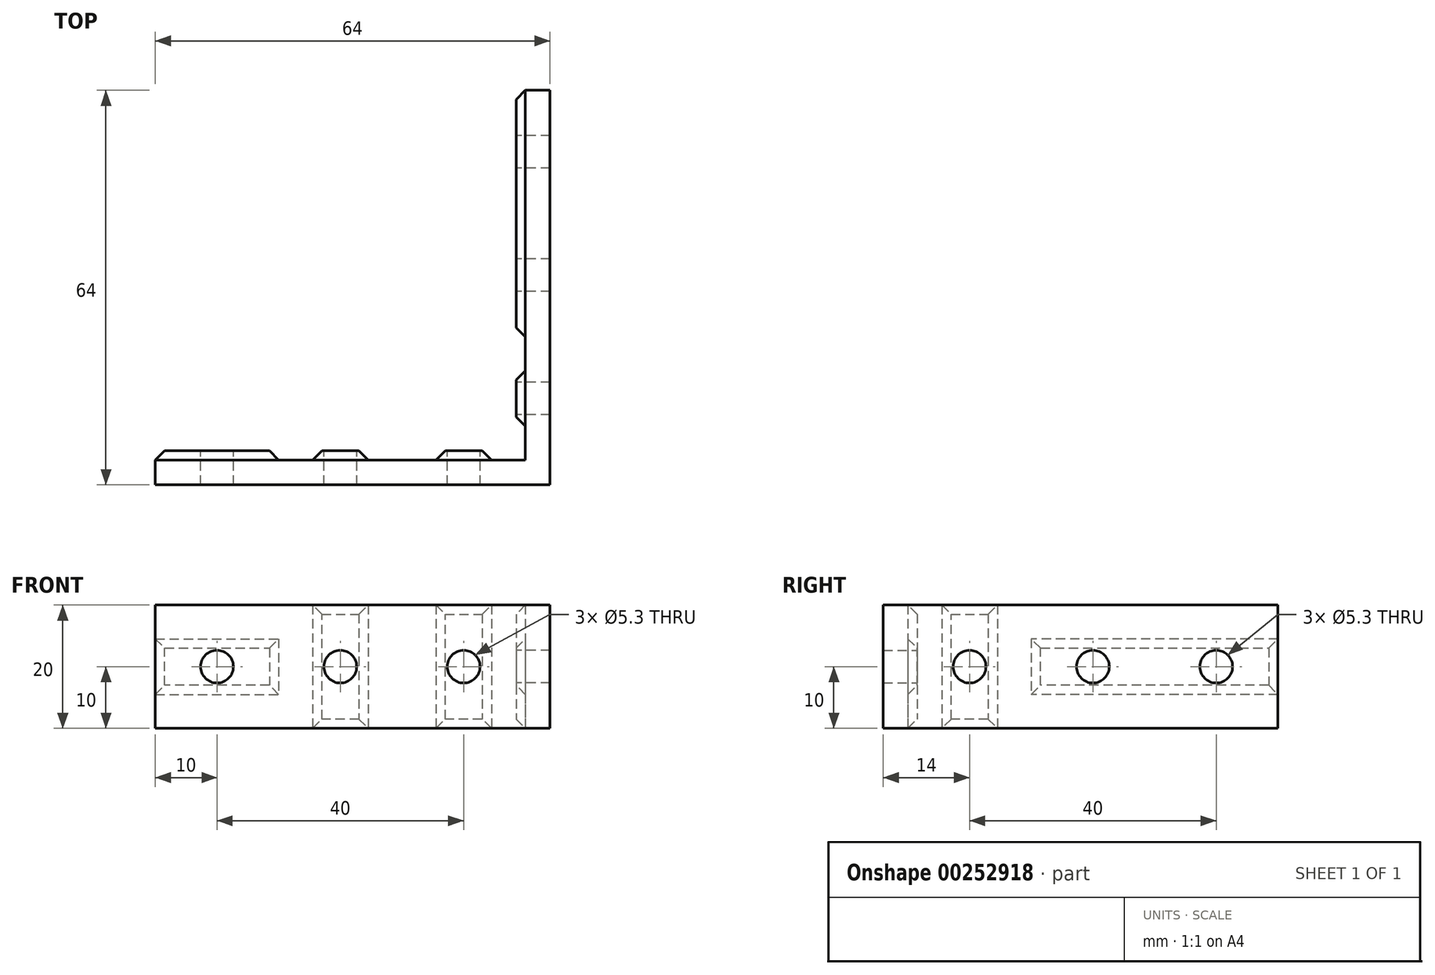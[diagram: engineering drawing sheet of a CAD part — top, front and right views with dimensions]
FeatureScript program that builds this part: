
annotation { "Feature Type Name" : "Feature", "Feature Type Description" : "" }
export const myFeature = defineFeature(function(context is Context, id is Id, definition is map)
    precondition{}
    {
        {
            var Q0;
            Q0=qCreatedBy(makeId("Top.planeOp"),FACE);
            var sketch = newSketch(context, id + "F0", { "sketchPlane" : qUnion([Q0])});
            skLineSegment(sketch, "E0", {"start": v(0, 0) * mm, "end": v(0, 64) * mm});
            skLineSegment(sketch, "E1", {"start": v(0, 64) * mm, "end": v(-4, 64) * mm});
            skLineSegment(sketch, "E2", {"start": v(-4, 64) * mm, "end": v(-4, 4) * mm});
            skLineSegment(sketch, "E3", {"start": v(-4, 4) * mm, "end": v(-64, 4) * mm});
            skLineSegment(sketch, "E4", {"start": v(-64, 4) * mm, "end": v(-64, 0) * mm});
            skLineSegment(sketch, "E5", {"start": v(-64, 0) * mm, "end": v(0, 0) * mm});
            skSolve(sketch);
        }
        {
            var Q0;
            Q0 = qSketchRegion(id + "F0", true);
            extrude(context, id + "F1", {"entities" : qUnion([Q0]), "depth" : 20 * mm});
        }
        {
            var Q0;
            Q0=makeQuery(id+"F1.opExtrude","SWEPT_FACE",FACE,{"disambiguationData":[OSD([sQuery(id+"F0.wireOp",EDGE,"E3")])]});
            var sketch = newSketch(context, id + "F2", { "sketchPlane" : qUnion([Q0])});
            skLineSegment(sketch, "E6.bottom", {"start": v(9.5, 20) * mm, "end": v(18.5, 20) * mm});
            skLineSegment(sketch, "E6.top", {"start": v(9.5, 0) * mm, "end": v(18.5, 0) * mm});
            skLineSegment(sketch, "E6.left", {"start": v(9.5, 20) * mm, "end": v(9.5, 0) * mm});
            skLineSegment(sketch, "E6.right", {"start": v(18.5, 20) * mm, "end": v(18.5, 0) * mm});
            skLineSegment(sketch, "E7.bottom", {"start": v(29.5, 20) * mm, "end": v(38.5, 20) * mm});
            skLineSegment(sketch, "E7.top", {"start": v(29.5, 0) * mm, "end": v(38.5, 0) * mm});
            skLineSegment(sketch, "E7.left", {"start": v(29.5, 20) * mm, "end": v(29.5, 0) * mm});
            skLineSegment(sketch, "E7.right", {"start": v(38.5, 20) * mm, "end": v(38.5, 0) * mm});
            skLineSegment(sketch, "E8.bottom", {"start": v(64, 14.5) * mm, "end": v(44, 14.5) * mm});
            skLineSegment(sketch, "E8.top", {"start": v(64, 5.5) * mm, "end": v(44, 5.5) * mm});
            skLineSegment(sketch, "E8.left", {"start": v(64, 14.5) * mm, "end": v(64, 5.5) * mm});
            skLineSegment(sketch, "E8.right", {"start": v(44, 14.5) * mm, "end": v(44, 5.5) * mm});
            skSolve(sketch);
        }
        {
            var Q0;
            Q0 = qSketchRegion(id + "F2", true);
            extrude(context, id + "F3", {"entities" : qUnion([Q0]), "operationType" : NewBodyOperationType.ADD, "depth" : 1.5 * mm});
        }
        {
            var Q0;
            Q0=makeQuery(id+"F1.opExtrude","SWEPT_FACE",FACE,{"disambiguationData":[OSD([sQuery(id+"F0.wireOp",EDGE,"E2")])]});
            var sketch = newSketch(context, id + "F4", { "sketchPlane" : qUnion([Q0])});
            skLineSegment(sketch, "E9.bottom", {"start": v(-64, 14.5) * mm, "end": v(-24, 14.5) * mm});
            skLineSegment(sketch, "E9.top", {"start": v(-64, 5.5) * mm, "end": v(-24, 5.5) * mm});
            skLineSegment(sketch, "E9.left", {"start": v(-64, 14.5) * mm, "end": v(-64, 5.5) * mm});
            skLineSegment(sketch, "E9.right", {"start": v(-24, 14.5) * mm, "end": v(-24, 5.5) * mm});
            skLineSegment(sketch, "E10.bottom", {"start": v(-9.5, 20) * mm, "end": v(-18.5, 20) * mm});
            skLineSegment(sketch, "E10.top", {"start": v(-9.5, 0) * mm, "end": v(-18.5, 0) * mm});
            skLineSegment(sketch, "E10.left", {"start": v(-9.5, 20) * mm, "end": v(-9.5, 0) * mm});
            skLineSegment(sketch, "E10.right", {"start": v(-18.5, 20) * mm, "end": v(-18.5, 0) * mm});
            skSolve(sketch);
        }
        {
            var Q0;
            Q0 = qSketchRegion(id + "F4", true);
            extrude(context, id + "F5", {"entities" : qUnion([Q0]), "operationType" : NewBodyOperationType.ADD, "depth" : 1.5 * mm});
        }
        {
            var Q0;
            Q0=makeQuery(id+"F5.opExtrude","CAP_EDGE",EDGE,{"disambiguationData":[OSD([sQuery(id+"F4.wireOp",EDGE,"E9.left")])],"isStart":false});
            var Q1;
            Q1=makeQuery(id+"F5.opExtrude","CAP_EDGE",EDGE,{"disambiguationData":[OSD([sQuery(id+"F4.wireOp",EDGE,"E9.bottom")])],"isStart":false});
            var Q2;
            Q2=makeQuery(id+"F5.opExtrude","CAP_EDGE",EDGE,{"disambiguationData":[OSD([sQuery(id+"F4.wireOp",EDGE,"E9.top")])],"isStart":false});
            var Q3;
            Q3=makeQuery(id+"F5.opExtrude","CAP_EDGE",EDGE,{"disambiguationData":[OSD([sQuery(id+"F4.wireOp",EDGE,"E9.right")])],"isStart":false});
            var Q4;
            Q4=makeQuery(id+"F3.opExtrude","CAP_EDGE",EDGE,{"disambiguationData":[OSD([sQuery(id+"F2.wireOp",EDGE,"E8.bottom")])],"isStart":false});
            var Q5;
            Q5=makeQuery(id+"F3.opExtrude","CAP_EDGE",EDGE,{"disambiguationData":[OSD([sQuery(id+"F2.wireOp",EDGE,"E8.top")])],"isStart":false});
            var Q6;
            Q6=makeQuery(id+"F3.opExtrude","CAP_EDGE",EDGE,{"disambiguationData":[OSD([sQuery(id+"F2.wireOp",EDGE,"E8.right")])],"isStart":false});
            var Q7;
            Q7=makeQuery(id+"F3.opExtrude","CAP_EDGE",EDGE,{"disambiguationData":[OSD([sQuery(id+"F2.wireOp",EDGE,"E8.left")])],"isStart":false});
            var Q8;
            Q8=makeQuery(id+"F3.opExtrude","CAP_FACE",FACE,{"disambiguationData":[OSD([sQuery(id+"F2.wireOp",EDGE,"E7.bottom"),sQuery(id+"F2.wireOp",EDGE,"E7.top"),sQuery(id+"F2.wireOp",EDGE,"E7.left"),sQuery(id+"F2.wireOp",EDGE,"E7.right")])],"isStart":false});
            var Q9;
            Q9=makeQuery(id+"F3.opExtrude","CAP_FACE",FACE,{"disambiguationData":[OSD([sQuery(id+"F2.wireOp",EDGE,"E6.bottom"),sQuery(id+"F2.wireOp",EDGE,"E6.top"),sQuery(id+"F2.wireOp",EDGE,"E6.left"),sQuery(id+"F2.wireOp",EDGE,"E6.right")])],"isStart":false});
            var Q10;
            Q10=makeQuery(id+"F5.opExtrude","CAP_FACE",FACE,{"disambiguationData":[OSD([sQuery(id+"F4.wireOp",EDGE,"E10.bottom"),sQuery(id+"F4.wireOp",EDGE,"E10.top"),sQuery(id+"F4.wireOp",EDGE,"E10.left"),sQuery(id+"F4.wireOp",EDGE,"E10.right")])],"isStart":false});
            chamfer(context, id + "F6", {"entities" : qUnion([Q0, Q1, Q2, Q3, Q4, Q5, Q6, Q7, Q8, Q9, Q10]), "width" : 1.5 * mm, "tangentPropagation" : true});
        }
        {
            var Q0;
            Q0=makeQuery(id+"F3.opExtrude","CAP_FACE",FACE,{"disambiguationData":[OSD([sQuery(id+"F2.wireOp",EDGE,"E6.bottom"),sQuery(id+"F2.wireOp",EDGE,"E6.top"),sQuery(id+"F2.wireOp",EDGE,"E6.left"),sQuery(id+"F2.wireOp",EDGE,"E6.right")])],"isStart":false});
            var sketch = newSketch(context, id + "F7", { "sketchPlane" : qUnion([Q0])});
            skCircle(sketch, "E11", {"center": v(14, 10) * mm, "radius": 2.65 * mm});
            skPoint(sketch, "E11.centerSnap0", {"position": v(17, 10) * mm});
            skPoint(sketch, "E11.centerSnap1", {"position": v(14, 18.5) * mm});
            skLineSegment(sketch, "E12.0.0", {"start": v(31, 18.5) * mm, "end": v(31, 1.5) * mm, "construction": true});
            skLineSegment(sketch, "E12.0.1", {"start": v(31, 1.5) * mm, "end": v(37, 1.5) * mm, "construction": true});
            skLineSegment(sketch, "E12.0.2", {"start": v(37, 1.5) * mm, "end": v(37, 18.5) * mm, "construction": true});
            skLineSegment(sketch, "E12.0.3", {"start": v(37, 18.5) * mm, "end": v(31, 18.5) * mm, "construction": true});
            skLineSegment(sketch, "E13.0.0", {"start": v(45.5, 13) * mm, "end": v(45.5, 7) * mm, "construction": true});
            skLineSegment(sketch, "E13.0.1", {"start": v(45.5, 7) * mm, "end": v(62.5, 7) * mm, "construction": true});
            skLineSegment(sketch, "E13.0.2", {"start": v(62.5, 7) * mm, "end": v(62.5, 13) * mm, "construction": true});
            skLineSegment(sketch, "E13.0.3", {"start": v(62.5, 13) * mm, "end": v(45.5, 13) * mm, "construction": true});
            skPoint(sketch, "E14.centerSnap0", {"position": v(37, 10) * mm});
            skPoint(sketch, "E14.centerSnap1", {"position": v(34, 18.5) * mm});
            skCircle(sketch, "E15", {"center": v(34, 10) * mm, "radius": 2.65 * mm});
            skCircle(sketch, "E16", {"center": v(54, 10) * mm, "radius": 2.65 * mm});
            skPoint(sketch, "E16.centerSnap0", {"position": v(54, 13) * mm});
            skPoint(sketch, "E16.centerSnap1", {"position": v(45.5, 10) * mm});
            skSolve(sketch);
        }
        {
            var Q0;
            Q0 = qSketchRegion(id + "F7", true);
            extrude(context, id + "F8", {"entities" : qUnion([Q0]), "operationType" : NewBodyOperationType.REMOVE, "endBound" : BoundingType.UP_TO_NEXT, "oppositeDirection" : true, "depth" : 25 * mm});
        }
        {
            var Q0;
            Q0=makeQuery(id+"F5.opExtrude","CAP_FACE",FACE,{"disambiguationData":[OSD([sQuery(id+"F4.wireOp",EDGE,"E9.bottom"),sQuery(id+"F4.wireOp",EDGE,"E9.top"),sQuery(id+"F4.wireOp",EDGE,"E9.left"),sQuery(id+"F4.wireOp",EDGE,"E9.right")])],"isStart":false});
            var sketch = newSketch(context, id + "F9", { "sketchPlane" : qUnion([Q0])});
            skCircle(sketch, "E17", {"center": v(-54, 10) * mm, "radius": 2.65 * mm});
            skPoint(sketch, "E17.centerSnap0", {"position": v(-62.5, 10) * mm});
            skCircle(sketch, "E18", {"center": v(-34, 10) * mm, "radius": 2.65 * mm});
            skLineSegment(sketch, "E19.0.0", {"start": v(-17, 18.5) * mm, "end": v(-17, 1.5) * mm, "construction": true});
            skLineSegment(sketch, "E19.0.1", {"start": v(-17, 1.5) * mm, "end": v(-11, 1.5) * mm, "construction": true});
            skLineSegment(sketch, "E19.0.2", {"start": v(-11, 1.5) * mm, "end": v(-11, 18.5) * mm, "construction": true});
            skLineSegment(sketch, "E19.0.3", {"start": v(-11, 18.5) * mm, "end": v(-17, 18.5) * mm, "construction": true});
            skCircle(sketch, "E20", {"center": v(-14, 10) * mm, "radius": 2.65 * mm});
            skPoint(sketch, "E20.centerSnap0", {"position": v(-17, 10) * mm});
            skPoint(sketch, "E20.centerSnap1", {"position": v(-14, 18.5) * mm});
            skSolve(sketch);
        }
        {
            var Q0;
            Q0 = qSketchRegion(id + "F9", true);
            extrude(context, id + "F10", {"entities" : qUnion([Q0]), "operationType" : NewBodyOperationType.REMOVE, "endBound" : BoundingType.UP_TO_NEXT, "oppositeDirection" : true, "depth" : 25 * mm});
        }
    });
